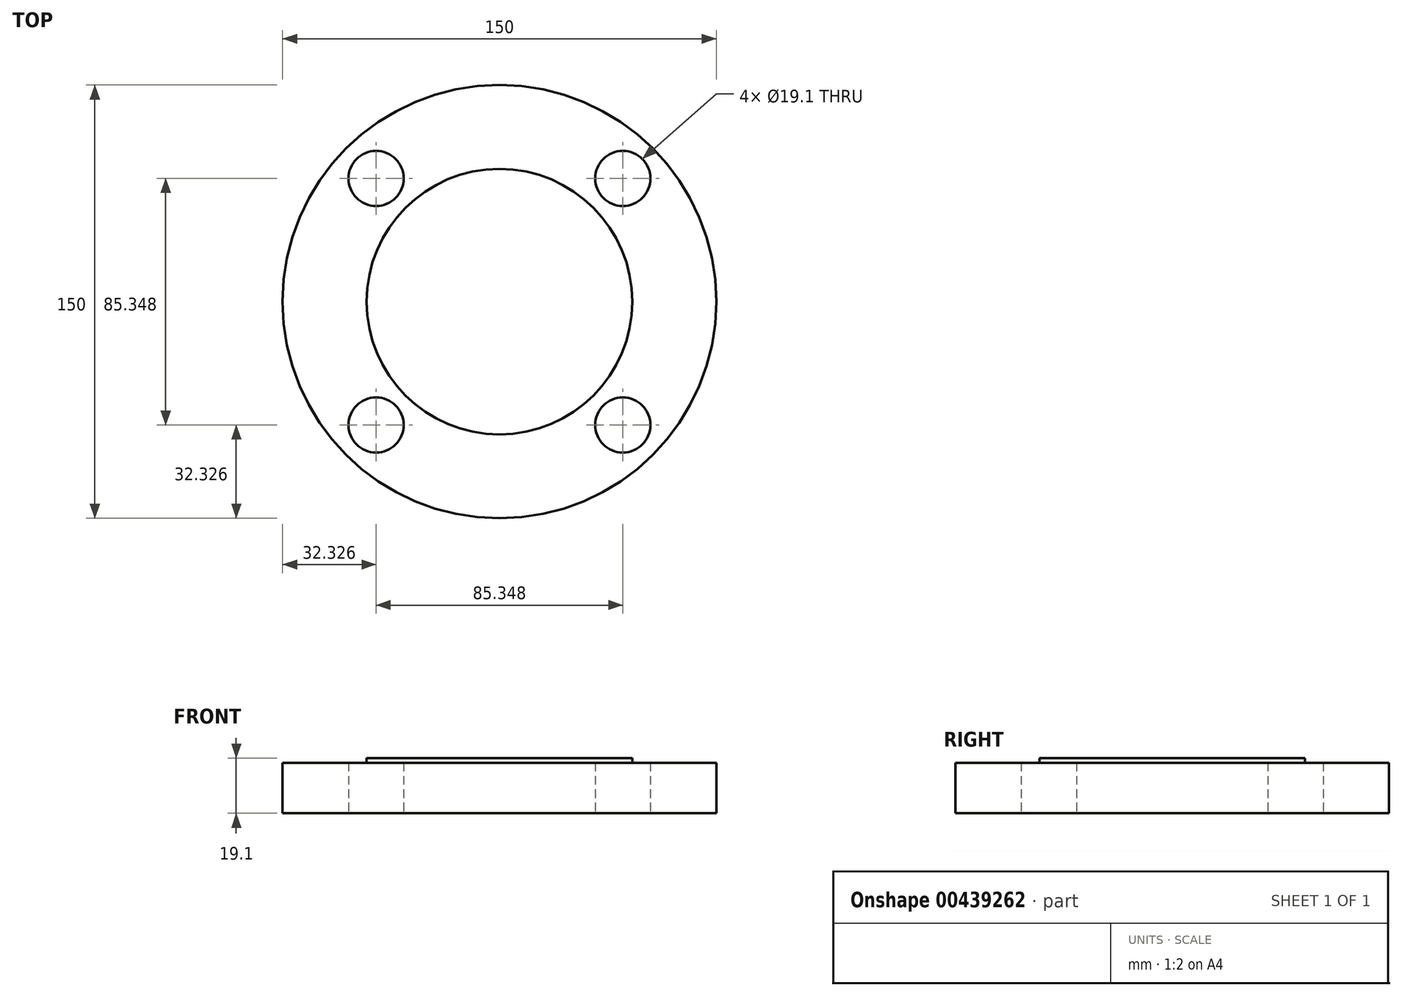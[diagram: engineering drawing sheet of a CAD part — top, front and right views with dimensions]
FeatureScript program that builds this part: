
annotation { "Feature Type Name" : "Feature", "Feature Type Description" : "" }
export const myFeature = defineFeature(function(context is Context, id is Id, definition is map)
    precondition{}
    {
        {
            assignVariable(context, id + "F0", {"name" : "THK", "anyValue" : 17.5});
        }
        {
            assignVariable(context, id + "F1", {"name" : "B", "anyValue" : 19.1});
        }
        {
            var Q0;
            Q0=qCreatedBy(makeId("Top.planeOp"),FACE);
            var sketch = newSketch(context, id + "F2", { "sketchPlane" : qUnion([Q0])});
            skCircle(sketch, "E0", {"center": v(0, 0) * mm, "radius": 60.35 * mm, "construction": true});
            skCircle(sketch, "E1", {"center": v(0, 0) * mm, "radius": 45.95 * mm});
            skCircle(sketch, "E2", {"center": v(0, 0) * mm, "radius": 75 * mm});
            skLineSegment(sketch, "E3", {"start": v(0, 0) * mm, "end": v(0, -170) * mm, "construction": true});
            skLineSegment(sketch, "E4", {"start": v(0, 0) * mm, "end": v(42.67, -42.67) * mm, "construction": true});
            skCircle(sketch, "E5", {"center": v(42.67, -42.67) * mm, "radius": 9.55 * mm});
            skCircle(sketch, "E6.1.0", {"center": v(42.67, 42.67) * mm, "radius": 9.55 * mm});
            skCircle(sketch, "E6.2.0", {"center": v(-42.67, 42.67) * mm, "radius": 9.55 * mm});
            skCircle(sketch, "E6.3.0", {"center": v(-42.67, -42.67) * mm, "radius": 9.55 * mm});
            skSolve(sketch);
        }
        {
            var Q0;
            Q0=makeQuery(id+"F2.imprint","IMPRINT",FACE,{"disambiguationData":[TD([[makeQuery(id+"F2.imprint","IMPRINT",EDGE,{"derivedFrom":sQuery(id+"F2.wireOp",EDGE,"E1")}),1.0]])]});
            var sketch = newSketch(context, id + "F3", { "sketchPlane" : qUnion([Q0])});
            skArc(sketch, "E7", {"start": v(-36.18, -30) * mm, "mid": v(0, -47) * mm, "end": v(36.18, -30) * mm});
            skLineSegment(sketch, "E8", {"start": v(-75, -60) * mm, "end": v(-75, -170) * mm});
            skLineSegment(sketch, "E9", {"start": v(75, -170) * mm, "end": v(75, -60) * mm});
            skLineSegment(sketch, "E10", {"start": v(-75, -170) * mm, "end": v(75, -170) * mm});
            skLineSegment(sketch, "E11", {"start": v(-57.68, -30) * mm, "end": v(-36.18, -30) * mm});
            skLineSegment(sketch, "E12.trimOffspring", {"start": v(36.18, -30) * mm, "end": v(57.68, -30) * mm});
            skLineSegment(sketch, "E13", {"start": v(-57.68, -30) * mm, "end": v(-75, -60) * mm});
            skLineSegment(sketch, "E14", {"start": v(-75, -60) * mm, "end": v(75, -60) * mm, "construction": true});
            skLineSegment(sketch, "E15", {"start": v(75, -60) * mm, "end": v(57.68, -30) * mm});
            skSolve(sketch);
        }
        {
            var Q0;
            Q0=makeQuery(id+"F2.imprint","IMPRINT",FACE,{"disambiguationData":[TD([[makeQuery(id+"F2.imprint","IMPRINT",EDGE,{"derivedFrom":sQuery(id+"F2.wireOp",EDGE,"E1")}),-1.0]])]});
            extrude(context, id + "F4", {"entities" : qUnion([Q0]), "depth" : (getVariable(context, 'THK')) * mm, "offsetDistance" : 25 * mm});
        }
        {
            var Q0;
            {var subQ0=sQuery(id+"F3.wireOp",EDGE,"E7");Q0=makeQuery(id+"F3.imprint","IMPRINT",FACE,{"disambiguationData":[TD([[makeQuery(id+"F3.imprint","IMPRINT",EDGE,{"derivedFrom":subQ0}),1.0]])]});}
            var Q1;
            Q1=makeQuery(id+"F2.imprint","IMPRINT",FACE,{"disambiguationData":[TD([[makeQuery(id+"F2.imprint","IMPRINT",EDGE,{"derivedFrom":sQuery(id+"F2.wireOp",EDGE,"E1")}),1.0]])]});
            extrude(context, id + "F5", {"entities" : qUnion([Q0, Q1]), "operationType" : NewBodyOperationType.ADD, "depth" : (getVariable(context, 'B')) * mm, "offsetDistance" : 25 * mm});
        }
    });
